# Revit family: ef-20_30uys(q)2_uas(q)2_ubs(q)2_60Hz
name_source: partatom
category: 機械設備
units: mm (PartAtom-declared; Revit-internal decimal feet)

## family parameters
OmniClass タイトル = Industrial Ventilating Equipment
OmniClass 番号 = 23.75.35.21.17
パーツ タイプ = 標準
ロード時にボイドで切り取り = はい
丸型コネクタ寸法 = 直径を使用
作業面ベース = いいえ
共有 = いいえ
常に垂直 = はい
部屋計算ポイント = はい

## types (6) — shared parameters
Box_Angle = 46.00°
IfcExportAs = IfcFanType
IfcExportType = TUBEAXIAL
MID風量 = 0.0 m³/h
MIN風量 = 0.0 m³/h
OmniClassCode = 23-33 31 19 11 17
URL = https://www.mitsubishielectric.co.jp
Uniclass2015Code = Pr_65_67_29_67
Uniclass2015Title = Propeller fans
Uniclass2015Version = Systems v1.9
オリフィス_Depth = 50  [stored 0.164042 ft]
ファンの種類 = 軸流羽根
フレームの厚さ = 10  [stored 0.0328084 ft]
ボックス_Depth = 99  [stored 0.324803 ft]
ボックス_Height = 63  [stored 0.206693 ft]
ボックス_Width = 40  [stored 0.131234 ft]
仕様書バージョン = Version1.0
企業コード = 108420
分類コード = 50052503100110
周波数 = 60 Hz
呼称 = 有圧扇
極 = 4
極数 = 2
法定耐用年数 = 15
相 = 1
製品リリース年月 = 2022年6月1日
製品出荷対象 = 国内
製造元 = 三菱電機株式会社
設置方法 = 壁付
負荷分類 = 3_ファン類
運転質量 = 0.00 kg
電圧 = 100 V

## per-type parameters (varying)
| type | Box_H | Box_W | Depth | Height | MAX風量 | Width | オリフィス径 | 価格 | 消費電力 | 羽根径 | 製品質量 | 説明 | 質量 | 電動機出力 |
| EF-20UYS2 | 26 | 95 | 105  [stored 0.344488 ft] | 320  [stored 1.04987 ft] | 850.0 m³/h | 320  [stored 1.04987 ft] | 260  [stored 0.853018 ft] | 42500 $ | 39 W | ∅200 | 2.30 kg | 産業用有圧換気扇 機器冷却用 排気専用 排気形 | 2.76 kg | 20 W |
| EF-25UAS2 | 28 | 118 | 115  [stored 0.377297 ft] | 370  [stored 1.21391 ft] | 1430.0 m³/h | 370  [stored 1.21391 ft] | 305  [stored 1.00066 ft] | 45400 $ | 58 W | ∅250 | 3.30 kg | 産業用有圧換気扇 機器冷却用 排気専用 排気形 | 3.96 kg | 35 W |
| EF-30UBS2 | 30 | 144  [stored 0.472441 ft] | 125  [stored 0.410105 ft] | 420  [stored 1.37795 ft] | 2220.0 m³/h | 420  [stored 1.37795 ft] | 340  [stored 1.11549 ft] | 58000 $ | 95 W | ∅300 | 4.80 kg | 産業用有圧換気扇 機器冷却用 排気専用 排気形 | 5.76 kg | 65 W |
| EF-20UYSQ2 | 26 | 95 | 105  [stored 0.344488 ft] | 320  [stored 1.04987 ft] | 790.0 m³/h | 320  [stored 1.04987 ft] | 260  [stored 0.853018 ft] | 44500 $ | 37 W | ∅200 | 2.30 kg | 産業用有圧換気扇 機器冷却用 排気専用 給気形 | 2.76 kg | 20 W |
| EF-25UASQ2 | 28 | 118 | 115  [stored 0.377297 ft] | 370  [stored 1.21391 ft] | 1400.0 m³/h | 370  [stored 1.21391 ft] | 305  [stored 1.00066 ft] | 47800 $ | 57 W | ∅250 | 3.30 kg | 産業用有圧換気扇 機器冷却用 排気専用 給気形 | 3.96 kg | 35 W |
| EF-30UBSQ2 | 30 | 144  [stored 0.472441 ft] | 125  [stored 0.410105 ft] | 420  [stored 1.37795 ft] | 2200.0 m³/h | 420  [stored 1.37795 ft] | 340  [stored 1.11549 ft] | 60900 $ | 93 W | ∅300 | 4.80 kg | 産業用有圧換気扇 機器冷却用 排気専用 給気形 | 5.76 kg | 65 W |

note: column(s) folded — value = type name in every type: モデル

note: [stored X ft] marks values corroborated as IEEE doubles in the binary element streams (Revit-internal decimal feet)
